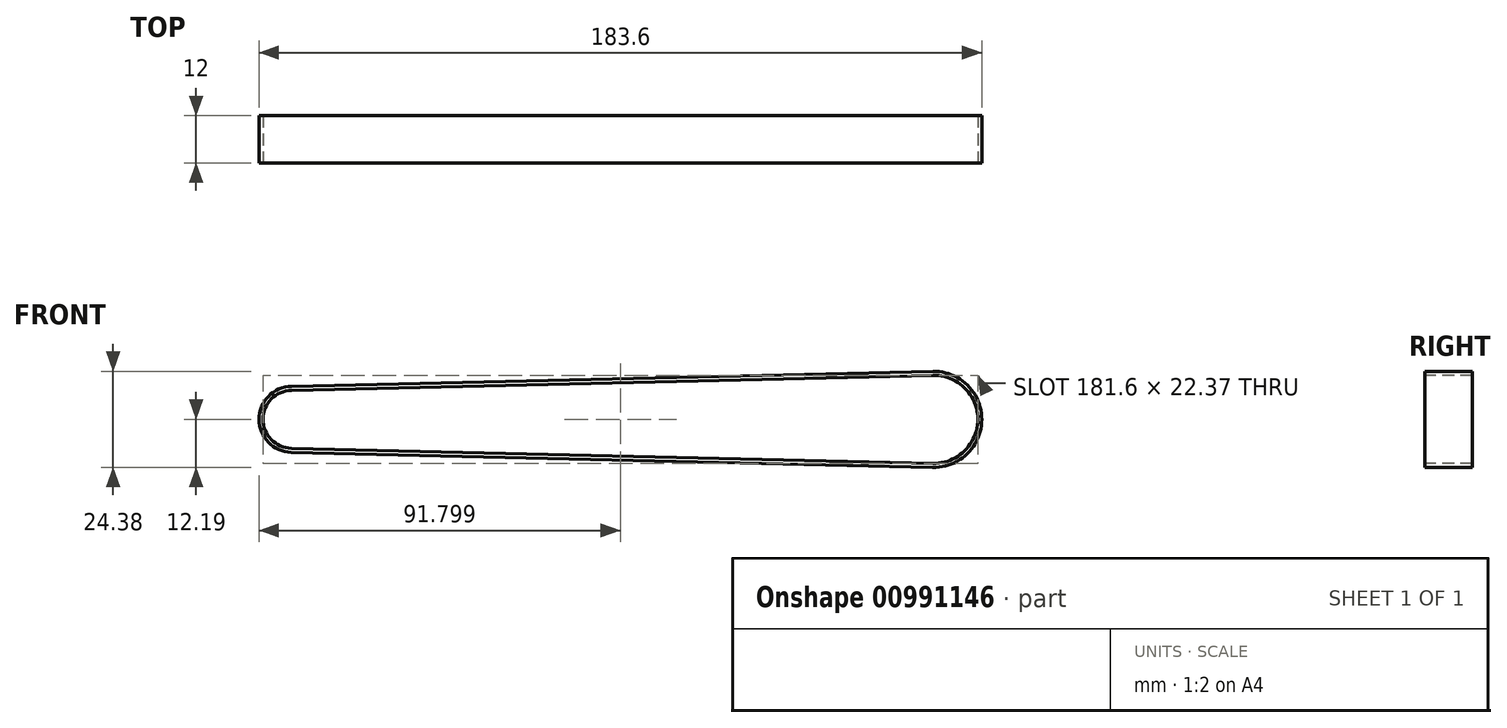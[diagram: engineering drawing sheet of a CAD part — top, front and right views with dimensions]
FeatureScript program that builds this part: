
annotation { "Feature Type Name" : "Feature", "Feature Type Description" : "" }
export const myFeature = defineFeature(function(context is Context, id is Id, definition is map)
    precondition{}
    {
        {
            var Q0;
            Q0=qCreatedBy(makeId("Front.planeOp"),FACE);
            var sketch = newSketch(context, id + "F0", { "sketchPlane" : qUnion([Q0])});
            skArc(sketch, "E0", {"start": v(-36.43, 7.3) * mm, "mid": v(-43.55, 0) * mm, "end": v(-36.43, -7.3) * mm});
            skArc(sketch, "E1", {"start": v(126.53, -11.1) * mm, "mid": v(137.9, 0) * mm, "end": v(126.53, 11.1) * mm});
            skLineSegment(sketch, "E2", {"start": v(-36.43, 7.3) * mm, "end": v(126.53, 11.1) * mm});
            skLineSegment(sketch, "E3", {"start": v(-36.43, -7.3) * mm, "end": v(126.53, -11.1) * mm});
            skSolve(sketch);
        }
        {
            var Q0;
            Q0=qCreatedBy(makeId("Right.planeOp"),FACE);
            var Q1;
            Q1=sQuery(id+"F0.wireOp",VERTEX,"E1.end");
            cPlane(context, id + "F1", {"entities" : qUnion([Q0, Q1]), "cplaneType" : CPlaneType.PLANE_POINT, "offset" : 25 * mm, "width" : 150 * mm, "height" : 150 * mm});
        }
        {
            var Q0;
            Q0=qCreatedBy(id+"F1.planeOp",FACE);
            var sketch = newSketch(context, id + "F2", { "sketchPlane" : qUnion([Q0])});
            skLineSegment(sketch, "E4", {"start": v(0, 11.18) * mm, "end": v(6, 11.18) * mm});
            skLineSegment(sketch, "E5", {"start": v(6, 11.18) * mm, "end": v(6, 12.18) * mm});
            skLineSegment(sketch, "E6", {"start": v(6, 12.18) * mm, "end": v(0, 12.18) * mm});
            skLineSegment(sketch, "E7.MirrorCS", {"start": v(-6, 12.18) * mm, "end": v(0, 12.18) * mm});
            skLineSegment(sketch, "E8.MirrorCS", {"start": v(0, 11.18) * mm, "end": v(-6, 11.18) * mm});
            skLineSegment(sketch, "E9.MirrorCS", {"start": v(-6, 11.18) * mm, "end": v(-6, 12.18) * mm});
            skSolve(sketch);
        }
        {
            var Q0;
            Q0=makeQuery(id+"F2.imprint","IMPRINT",FACE,{"disambiguationData":[TD([[makeQuery(id+"F2.imprint","IMPRINT",EDGE,{"derivedFrom":sQuery(id+"F2.wireOp",EDGE,"E4")}),1.0]])]});
            var Q1;
            Q1=sQuery(id+"F0.wireOp",EDGE,"E2");
            var Q2;
            Q2=sQuery(id+"F0.wireOp",EDGE,"E1");
            var Q3;
            Q3=sQuery(id+"F0.wireOp",EDGE,"E3");
            var Q4;
            Q4=sQuery(id+"F0.wireOp",EDGE,"E0");
            sweep(context, id + "F3", {"profiles" : qUnion([Q0]), "path" : qUnion([Q1, Q2, Q3, Q4])});
        }
    });
